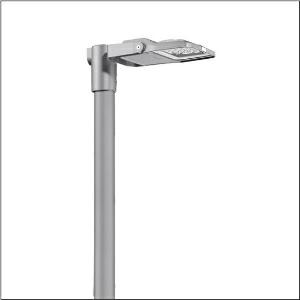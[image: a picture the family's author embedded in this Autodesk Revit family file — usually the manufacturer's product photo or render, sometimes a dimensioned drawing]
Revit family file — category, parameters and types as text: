
# Revit family: floodlight_fl_21_iq_micro___pl52_5xa7762a4d3a_1d61
name_source: partatom
category: Lighting Fixtures
units: mm (PartAtom-declared; Revit-internal decimal feet)

## family parameters
Cut with Voids When Loaded = No
Host = Face
Light Source = No
Part Type = Normal
Room Calculation Point = No
Round Connector Dimension = Use Diameter
Shared = No

## types (1)
- --- (1 x LED, 3010 lm, 23.1 W, 4000K)
    Apparent Load = 23 VA
    CIE Flux Codes = 26 60 98 100 100
    Color Rendering = 70
    Color Temperature = 4000K
    Default Elevation = 1800 mm
    Description = Floodlight FL 21 iQ micro, floodlight, primary light control with lens, of PMMA, primary optical cover: protective disc, of toughened safety glass, transparent, light distribution: PL52, light emission: direct distribution, installation type: surface-mounted, LED, High Power LED, rated luminous flux: 3.010lm, luminous efficacy: 130lm/W, light colour: 740, colour temperature: 4000K, control: Auto-Match, Temp-Guard, Night-Set, Smart-Wire, Desk-Remote (wireless, voltage-free reading and setting of iQ features in the workshop via application-optimized NFC function/RFID function), optimised constant luminous flux control (CLO 2.0), Street-Remote, with terminal, 6-pole, mains connection: 220..240V, AC, 50/60Hz, start of lifetime: 23W, end of service life: 24W, reduction: 11W, luminaire housing, of diecast aluminium, powder-coated, Siteco® metallic grey (DB 702S), corrosivity category C5 mid according to DIN EN ISO 12944, sealing non-destructively replaceable, please order mast flange separately, mast bracket, of steel, galvanised, powder-coated, Siteco® metallic grey (DB 702S), protection rating (complete): IP66, insulation class (complete): insulation class II (safety insulation), certification: CE, ENEC, VDE, protection symbol: D, impact resistance: IK07, permissible operating ambient temperature: -40..+40°C, permissible operating ambient temperature for outdoor applications: -40..+50°C, standard: DIN EN 12944, LABS conformity tested according to VDMA 24364:2018-05, packaging unit: 1 piece

Light Distribution: PL52
    Height = 65 mm
    Lamp = 1 x LED
    Lamp Light Flux = 3010 lm
    Lamp Power = 23.1 W
    Lamp count = 1
    Length = 312 mm
    Luminous efficacy = 130 lm/W
    Manufacturer = Siteco
    ModVariant = No
    Model = 5XA7762A4D3A
    Number of Poles = 1
    OnlyDefault = Yes
    Power Factor = 1
    Product Name = Floodlight FL 21 iQ micro | PL52
    Product group = floodlight | pylon annexe
    ProductGroupID = 6200
    Protection Class = Protection class II
    Protection Degree = IP 66
    RLX_Detail_Level = 1
    RLX_Emergency_Light_Flux = 0 lm
    RLX_Emergency_Type = 0
    RLX_Emergency_Type_DB = No
    RlxData = <blob elided: 101837 chars, md5=08aa936d>
    Socket = socket
    Standby Power = 0 W
    System Light Flux = 3010 lm
    System Power = 23 W
    Type Comments = factory setting: luminous flux: 100 % | dim-lin: 254 | 455 mA
    Type Image = l_1007121.jpg
    URL = http://relux.com
    VarID = @adj_128923
    Voltage = 0 V
    Weight = 0.00 kg
    Width = 230 mm

## geometry (parser evidence)
native form markers: Blend x4, Sweep x11
no freeform markers — native parametric forms only
